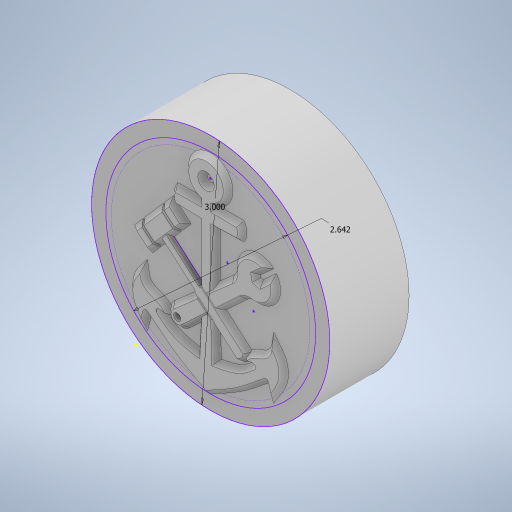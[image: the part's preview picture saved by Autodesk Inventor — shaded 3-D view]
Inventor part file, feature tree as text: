
AUTODESK INVENTOR PART (.ipt)
format: ipt  version: 2024 (Build 280153000, 153)  size: 625,664 bytes
history: native  units: in
note: dims shown in document units (in); Inventor stores cm internally (conversion verified against a paired STEP export)
features: extrude x3, sketch x2, chamfer x1
ambient origin geometry x8: Origin, YZ Plane, XZ Plane, XY Plane, X Axis, Y Axis, Z Axis, Center Point
bodies: Body1 (feature_tree)
feature tree (6):
  sketch  "Sketch4"  dims[d4=0.125in d5=0.0in d7=1.0in d8=0.0in]
  extrude  "Extrusion3"  Depth=1.0in TaperAngle=0.0deg
  extrude  "Extrusion4"  Depth=12.0in TaperAngle=0.0deg
  chamfer  "Chamfer1"  Distance=2.6417in
  extrude  "Extrusion5"  Depth=3.0in
  sketch  "Sketch5"  dims[d9=0.06in d10=0.125in d11=45.0deg d12=12.0in d13=0.0in d14=2.6417in d15=3.0in]
